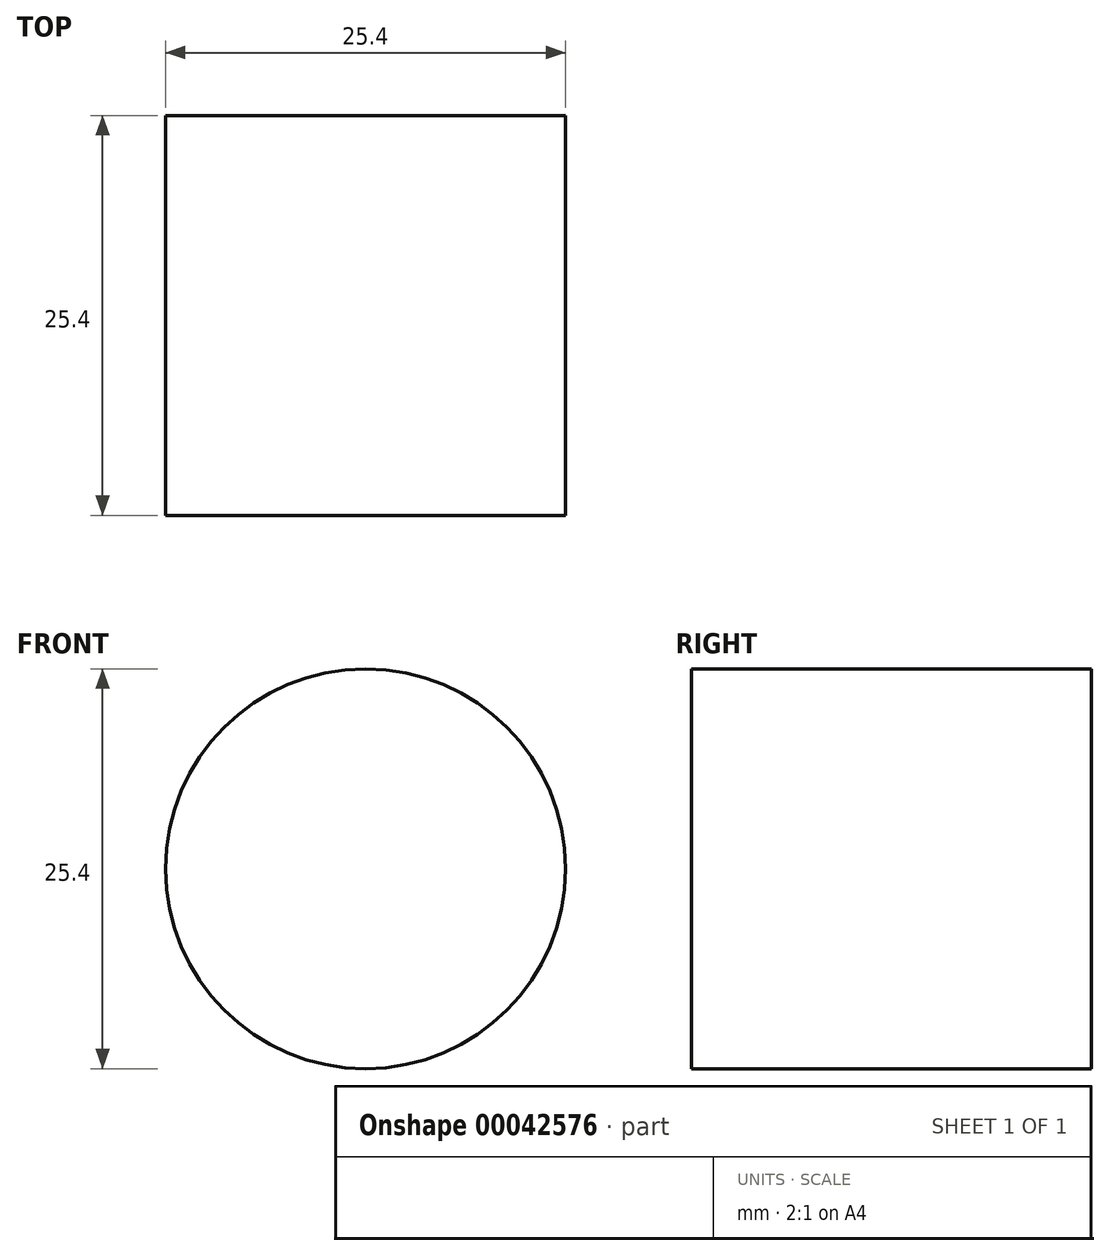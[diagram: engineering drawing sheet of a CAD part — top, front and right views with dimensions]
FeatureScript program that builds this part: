
annotation { "Feature Type Name" : "Feature", "Feature Type Description" : "" }
export const myFeature = defineFeature(function(context is Context, id is Id, definition is map)
    precondition{}
    {
        {
            var Q0;
            Q0=qCreatedBy(makeId("Front.planeOp"),FACE);
            var sketch = newSketch(context, id + "F0", { "sketchPlane" : qUnion([Q0])});
            skCircle(sketch, "E0", {"center": v(0, 0) * mm, "radius": 12.7 * mm});
            skSolve(sketch);
        }
        {
            var Q0;
            Q0 = qSketchRegion(id + "F0", true);
            extrude(context, id + "F1", {"entities" : qUnion([Q0]), "depth" : 25.4 * mm});
        }
    });
